# Revit family: Pantalla Modelo NX7
name_source: partatom
category: Luminarias
units: mm (PartAtom-declared; Revit-internal decimal feet)

## family parameters
Compartido = No
Corte con vacíos al cargar = No
Cota de conector redondo = Diámetro de uso
Origen de luz = No
Punto de cálculo de habitación = No
Se basa en plano de trabajo = Sí
Siempre vertical = No
Tipo de pieza = Normal

## types (2) — shared parameters
Comentarios de vataje = 100-240V
Espesor = 60 mm  [stored 0.19685 ft]
Fabricante = BRILLANT
Modulo alto = 500 mm  [stored 1.64042 ft]
Modulo largo = 500 mm  [stored 1.64042 ft]
zero-valued in all types: Elevación por defecto

## per-type parameters (varying)
| type | Descripción | Modelo | Watt per fixture |
| Pantalla Modelo NX7_NX7180W.1 | PANTALLA DE PISO MODELO NX7, SIN OPCION DE MODELO INTERACTIVO, PIXEL PITCH 7.8MM, RESOLUCION DEL PANEL 64X64 DOTS, CANTIDAD/PANEL LED 4096 DOTS, CONFIGURACION DEL PIXEL SMD 3 EN 1, BRILLO DE 2300 NITS, ACTUALIZACION EN 1920 Hz, CONSUMO MAXIMO POR PANEL 180W Y PROMEDIO 110W, ESCALA DE GRISES 14BIT, AJUSTE DE BRILLO 256 NIVELES, CAPACIDAD MAXIMA DE CARGA 1200KG/M2, DIMENSION DEL PANEL 500X500X60MM CON UN AREA DE 0.25M2, ANGULO DE VISION 140/110 GRADOS, CONTRASTE 2000:1, IP 54, DURACION DE LUCES (50% BRILLO) >50,000 HORAS, TEMPERATURA DE OPERACIÓN -10C +40C, HUMEDAD DE OPERACIÓN 10%-90% RH, VOLTAJE AC 100-240V/50-60Hz, MODO DE ENTRADA CON CORRIENTE CONSTANTE, TIPO DE SEÑAL: AV/S-VIDEO/VGA/CVBS/HDMI/DVI/SDI. | NX7180W.1 | 180 |
| Pantalla Modelo NX7_NX7S180W.1 | PANTALLA DE PISO MODELO NX7S, CON OPCION DE MODELO INTERACTIVO, PIXEL PITCH 7.8MM, RESOLUCION DEL PANEL 64X64 DOTS, CANTIDAD/PANEL LED 4096 DOTS, CONFIGURACION DEL PIXEL SMD 3 EN 1, BRILLO DE 2300 NITS, ACTUALIZACION EN 1920 Hz, CONSUMO MAXIMO POR PANEL 200W Y PROMEDIO 120W, ESCALA DE GRISES 14BIT, AJUSTE DE BRILLO 256 NIVELES, CAPACIDAD MAXIMA DE CARGA 1200KG/M2, DIMENSION DEL PANEL 500X500X60MM CON UN AREA DE 0.25M2, ANGULO DE VISION 140/110 GRADOS, CONTRASTE 2000:1, IP 54, DURACION DE LUCES (50% BRILLO) >50,000 HORAS, TEMPERATURA DE OPERACIÓN -10C +40C, HUMEDAD DE OPERACIÓN 10%-90% RH, VOLTAJE AC 100-240V/50-60Hz, MODO DE ENTRADA CON CORRIENTE CONSTANTE, TIPO DE SEÑAL: AV/S-VIDEO/VGA/CVBS/HDMI/DVI/SDI. | NX7S180W.1 | 200 |

note: [stored X ft] marks values corroborated as IEEE doubles in the binary element streams (Revit-internal decimal feet)

## geometry (parser evidence)
native form markers: Blend x2
no freeform markers — native parametric forms only
